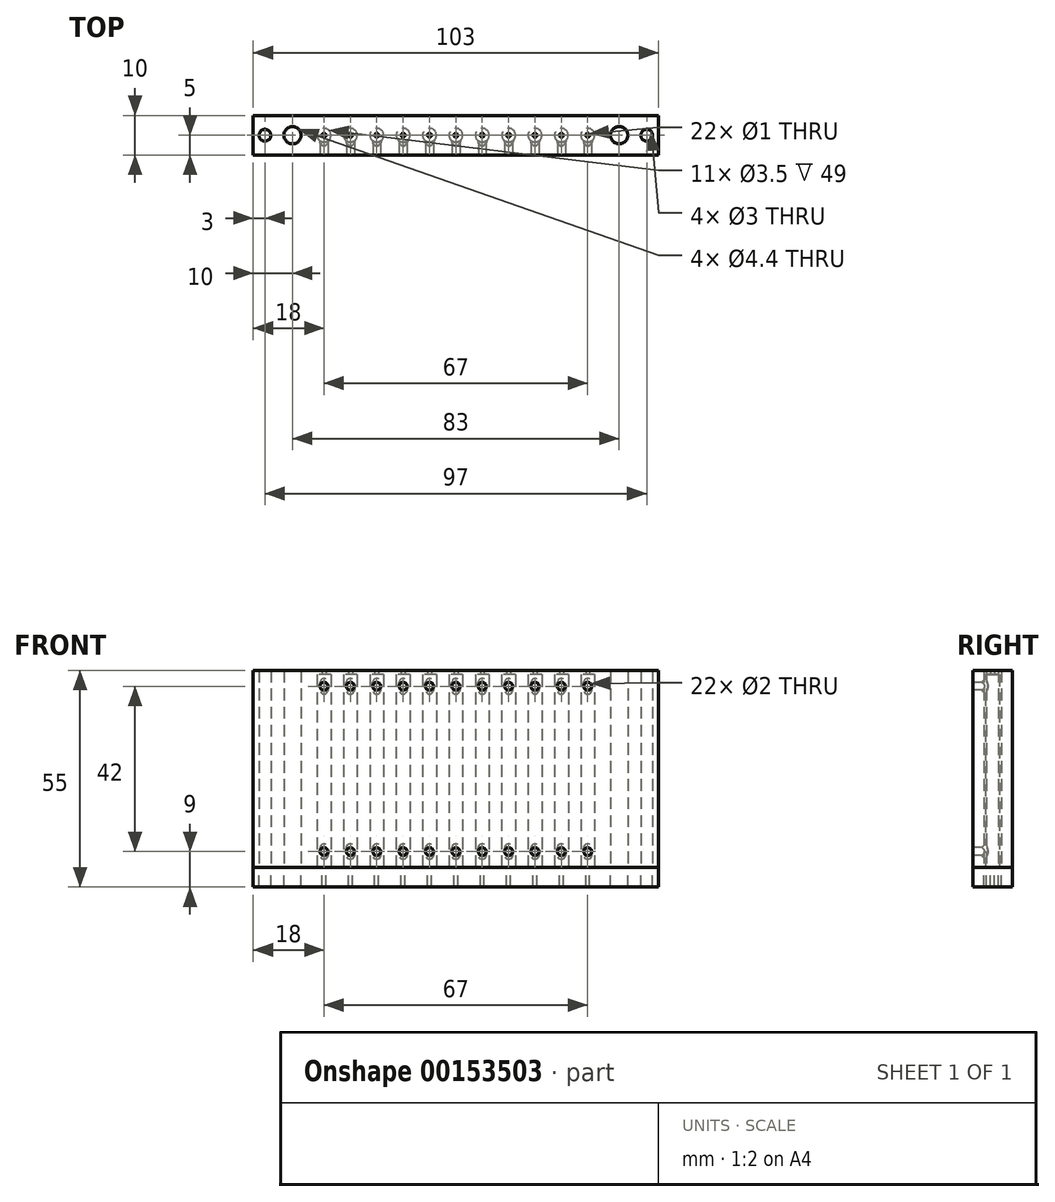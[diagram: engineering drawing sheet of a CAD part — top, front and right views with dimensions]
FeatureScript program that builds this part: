
annotation { "Feature Type Name" : "Feature", "Feature Type Description" : "" }
export const myFeature = defineFeature(function(context is Context, id is Id, definition is map)
    precondition{}
    {
        {
            var Q0;
            Q0=qCreatedBy(makeId("Top.planeOp"),FACE);
            var sketch = newSketch(context, id + "F0", { "sketchPlane" : qUnion([Q0])});
            skLineSegment(sketch, "E0.bottom", {"start": v(0, 0) * mm, "end": v(103, 0) * mm});
            skLineSegment(sketch, "E0.top", {"start": v(0, 10) * mm, "end": v(103, 10) * mm});
            skLineSegment(sketch, "E0.left", {"start": v(0, 0) * mm, "end": v(0, 10) * mm});
            skLineSegment(sketch, "E0.right", {"start": v(103, 0) * mm, "end": v(103, 10) * mm});
            skLineSegment(sketch, "E1", {"start": v(0, 5) * mm, "end": v(103, 5) * mm, "construction": true});
            skCircle(sketch, "E2", {"center": v(3, 5) * mm, "radius": 1.5 * mm});
            skCircle(sketch, "E3", {"center": v(10, 5) * mm, "radius": 2.2 * mm});
            skCircle(sketch, "E4", {"center": v(18, 5) * mm, "radius": 0.5 * mm});
            skLineSegment(sketch, "E5", {"start": v(51.5, 10) * mm, "end": v(51.5, 0) * mm, "construction": true});
            skCircle(sketch, "E6.MirrorC", {"center": v(93, 5) * mm, "radius": 2.2 * mm});
            skCircle(sketch, "E7.MirrorC", {"center": v(100, 5) * mm, "radius": 1.5 * mm});
            skCircle(sketch, "E8.1.0.0", {"center": v(24.7, 5) * mm, "radius": 0.5 * mm});
            skCircle(sketch, "E8.2.0.0", {"center": v(31.4, 5) * mm, "radius": 0.5 * mm});
            skCircle(sketch, "E8.3.0.0", {"center": v(38.1, 5) * mm, "radius": 0.5 * mm});
            skCircle(sketch, "E8.4.0.0", {"center": v(44.8, 5) * mm, "radius": 0.5 * mm});
            skCircle(sketch, "E8.5.0.0", {"center": v(51.5, 5) * mm, "radius": 0.5 * mm});
            skCircle(sketch, "E8.6.0.0", {"center": v(58.2, 5) * mm, "radius": 0.5 * mm});
            skCircle(sketch, "E8.7.0.0", {"center": v(64.9, 5) * mm, "radius": 0.5 * mm});
            skCircle(sketch, "E8.8.0.0", {"center": v(71.6, 5) * mm, "radius": 0.5 * mm});
            skCircle(sketch, "E8.9.0.0", {"center": v(78.3, 5) * mm, "radius": 0.5 * mm});
            skCircle(sketch, "E8.10.0.0", {"center": v(85, 5) * mm, "radius": 0.5 * mm});
            skLineSegment(sketch, "E8.direction1", {"start": v(17, 5) * mm, "end": v(24, 5) * mm, "construction": true});
            skCircle(sketch, "E9", {"center": v(10, 5) * mm, "radius": 5 * mm, "construction": true});
            skCircle(sketch, "E10", {"center": v(93, 5) * mm, "radius": 5 * mm, "construction": true});
            skSolve(sketch);
        }
        {
            var Q0;
            Q0=makeQuery(id+"F0.imprint","IMPRINT",FACE,{"disambiguationData":[TD([[makeQuery(id+"F0.imprint","IMPRINT",EDGE,{"derivedFrom":sQuery(id+"F0.wireOp",EDGE,"E0.bottom")}),1.0]])]});
            extrude(context, id + "F1", {"entities" : qUnion([Q0]), "depth" : 50 * mm});
        }
        {
            var Q0;
            Q0=makeQuery(id+"F0.imprint","IMPRINT",FACE,{"disambiguationData":[TD([[makeQuery(id+"F0.imprint","IMPRINT",EDGE,{"derivedFrom":sQuery(id+"F0.wireOp",EDGE,"E0.bottom")}),1.0]])]});
            var sketch = newSketch(context, id + "F2", { "sketchPlane" : qUnion([Q0])});
            skPoint(sketch, "E11.0", {"position": v(18, 5) * mm});
            skCircle(sketch, "E12", {"center": v(18, 5) * mm, "radius": 1.75 * mm});
            skCircle(sketch, "E13.1.0.0", {"center": v(24.7, 5) * mm, "radius": 1.75 * mm});
            skCircle(sketch, "E13.2.0.0", {"center": v(31.4, 5) * mm, "radius": 1.75 * mm});
            skCircle(sketch, "E13.3.0.0", {"center": v(38.1, 5) * mm, "radius": 1.75 * mm});
            skCircle(sketch, "E13.4.0.0", {"center": v(44.8, 5) * mm, "radius": 1.75 * mm});
            skCircle(sketch, "E13.5.0.0", {"center": v(51.5, 5) * mm, "radius": 1.75 * mm});
            skCircle(sketch, "E13.6.0.0", {"center": v(58.2, 5) * mm, "radius": 1.75 * mm});
            skCircle(sketch, "E13.7.0.0", {"center": v(64.9, 5) * mm, "radius": 1.75 * mm});
            skCircle(sketch, "E13.8.0.0", {"center": v(71.6, 5) * mm, "radius": 1.75 * mm});
            skCircle(sketch, "E13.9.0.0", {"center": v(78.3, 5) * mm, "radius": 1.75 * mm});
            skCircle(sketch, "E13.10.0.0", {"center": v(85, 5) * mm, "radius": 1.75 * mm});
            skLineSegment(sketch, "E13.direction1", {"start": v(18, 5) * mm, "end": v(24.7, 5) * mm, "construction": true});
            skSolve(sketch);
        }
        {
            var Q0;
            Q0 = qSketchRegion(id + "F2", true);
            extrude(context, id + "F3", {"entities" : qUnion([Q0]), "operationType" : NewBodyOperationType.REMOVE, "depth" : 49 * mm});
        }
        {
            var Q0;
            Q0=makeQuery(id+"F0.imprint","IMPRINT",FACE,{"disambiguationData":[TD([[makeQuery(id+"F0.imprint","IMPRINT",EDGE,{"derivedFrom":sQuery(id+"F0.wireOp",EDGE,"E0.bottom")}),1.0]])]});
            extrude(context, id + "F4", {"entities" : qUnion([Q0]), "oppositeDirection" : true, "depth" : 5 * mm});
        }
        {
            var Q0;
            Q0=makeQuery(id+"F1.opExtrude","SWEPT_FACE",FACE,{"disambiguationData":[OSD([sQuery(id+"F0.wireOp",EDGE,"E0.bottom")])]});
            var sketch = newSketch(context, id + "F5", { "sketchPlane" : qUnion([Q0])});
            skLineSegment(sketch, "E14.bottom", {"start": v(103, 50) * mm, "end": v(85, 50) * mm, "construction": true});
            skLineSegment(sketch, "E14.top", {"start": v(103, 46) * mm, "end": v(85, 46) * mm, "construction": true});
            skLineSegment(sketch, "E14.left", {"start": v(103, 50) * mm, "end": v(103, 46) * mm, "construction": true});
            skLineSegment(sketch, "E14.right", {"start": v(85, 50) * mm, "end": v(85, 46) * mm, "construction": true});
            skLineSegment(sketch, "E15", {"start": v(103, 25) * mm, "end": v(0, 25) * mm, "construction": true});
            skCircle(sketch, "E16", {"center": v(85, 46) * mm, "radius": 1 * mm});
            skCircle(sketch, "E17.0.1.0", {"center": v(85, 4) * mm, "radius": 1 * mm});
            skCircle(sketch, "E17.1.0.0", {"center": v(78.3, 46) * mm, "radius": 1 * mm});
            skCircle(sketch, "E17.1.1.0", {"center": v(78.3, 4) * mm, "radius": 1 * mm});
            skCircle(sketch, "E17.2.0.0", {"center": v(71.6, 46) * mm, "radius": 1 * mm});
            skCircle(sketch, "E17.2.1.0", {"center": v(71.6, 4) * mm, "radius": 1 * mm});
            skCircle(sketch, "E17.3.0.0", {"center": v(64.9, 46) * mm, "radius": 1 * mm});
            skCircle(sketch, "E17.3.1.0", {"center": v(64.9, 4) * mm, "radius": 1 * mm});
            skCircle(sketch, "E17.4.0.0", {"center": v(58.2, 46) * mm, "radius": 1 * mm});
            skCircle(sketch, "E17.4.1.0", {"center": v(58.2, 4) * mm, "radius": 1 * mm});
            skCircle(sketch, "E17.5.0.0", {"center": v(51.5, 46) * mm, "radius": 1 * mm});
            skCircle(sketch, "E17.5.1.0", {"center": v(51.5, 4) * mm, "radius": 1 * mm});
            skCircle(sketch, "E17.6.0.0", {"center": v(44.8, 46) * mm, "radius": 1 * mm});
            skCircle(sketch, "E17.6.1.0", {"center": v(44.8, 4) * mm, "radius": 1 * mm});
            skCircle(sketch, "E17.7.0.0", {"center": v(38.1, 46) * mm, "radius": 1 * mm});
            skCircle(sketch, "E17.7.1.0", {"center": v(38.1, 4) * mm, "radius": 1 * mm});
            skCircle(sketch, "E17.8.0.0", {"center": v(31.4, 46) * mm, "radius": 1 * mm});
            skCircle(sketch, "E17.8.1.0", {"center": v(31.4, 4) * mm, "radius": 1 * mm});
            skCircle(sketch, "E17.9.0.0", {"center": v(24.7, 46) * mm, "radius": 1 * mm});
            skCircle(sketch, "E17.9.1.0", {"center": v(24.7, 4) * mm, "radius": 1 * mm});
            skCircle(sketch, "E17.10.0.0", {"center": v(18, 46) * mm, "radius": 1 * mm});
            skCircle(sketch, "E17.10.1.0", {"center": v(18, 4) * mm, "radius": 1 * mm});
            skLineSegment(sketch, "E17.direction1", {"start": v(85, 46) * mm, "end": v(78.3, 46) * mm, "construction": true});
            skLineSegment(sketch, "E17.direction2", {"start": v(85, 46) * mm, "end": v(85, 4) * mm, "construction": true});
            skSolve(sketch);
        }
        {
            var Q0;
            Q0 = qSketchRegion(id + "F5", true);
            extrude(context, id + "F6", {"entities" : qUnion([Q0]), "operationType" : NewBodyOperationType.REMOVE, "oppositeDirection" : true, "depth" : 5 * mm});
        }
        {
            var Q0;
            Q0=makeQuery(id+"F6.boolean.opBoolean","COPY",EDGE,{"derivedFrom":makeQuery(id+"F6.opExtrude","CAP_EDGE",EDGE,{"disambiguationData":[OSD([sQuery(id+"F5.wireOp",EDGE,"E17.0.1.0")])],"isStart":true})});
            var Q1;
            Q1=makeQuery(id+"F6.boolean.opBoolean","COPY",EDGE,{"derivedFrom":makeQuery(id+"F6.opExtrude","CAP_EDGE",EDGE,{"disambiguationData":[OSD([sQuery(id+"F5.wireOp",EDGE,"E17.1.1.0")])],"isStart":true})});
            var Q2;
            Q2=makeQuery(id+"F6.boolean.opBoolean","COPY",EDGE,{"derivedFrom":makeQuery(id+"F6.opExtrude","CAP_EDGE",EDGE,{"disambiguationData":[OSD([sQuery(id+"F5.wireOp",EDGE,"E17.2.1.0")])],"isStart":true})});
            var Q3;
            Q3=makeQuery(id+"F6.boolean.opBoolean","INTERSECT",EDGE,{"derivedFrom":[makeQuery(id+"F3.boolean.opBoolean","COPY",FACE,{"derivedFrom":makeQuery(id+"F3.opExtrude","SWEPT_FACE",FACE,{"disambiguationData":[OSD([sQuery(id+"F2.wireOp",EDGE,"E13.10.0.0")])]})}),makeQuery(id+"F6.opExtrude","SWEPT_FACE",FACE,{"disambiguationData":[OSD([sQuery(id+"F5.wireOp",EDGE,"E17.0.1.0")])]})]});
            var Q4;
            Q4=makeQuery(id+"F6.boolean.opBoolean","INTERSECT",EDGE,{"derivedFrom":[makeQuery(id+"F3.boolean.opBoolean","COPY",FACE,{"derivedFrom":makeQuery(id+"F3.opExtrude","SWEPT_FACE",FACE,{"disambiguationData":[OSD([sQuery(id+"F2.wireOp",EDGE,"E13.9.0.0")])]})}),makeQuery(id+"F6.opExtrude","SWEPT_FACE",FACE,{"disambiguationData":[OSD([sQuery(id+"F5.wireOp",EDGE,"E17.1.1.0")])]})]});
            var Q5;
            Q5=makeQuery(id+"F6.boolean.opBoolean","INTERSECT",EDGE,{"derivedFrom":[makeQuery(id+"F3.boolean.opBoolean","COPY",FACE,{"derivedFrom":makeQuery(id+"F3.opExtrude","SWEPT_FACE",FACE,{"disambiguationData":[OSD([sQuery(id+"F2.wireOp",EDGE,"E13.8.0.0")])]})}),makeQuery(id+"F6.opExtrude","SWEPT_FACE",FACE,{"disambiguationData":[OSD([sQuery(id+"F5.wireOp",EDGE,"E17.2.1.0")])]})]});
            var Q6;
            Q6=makeQuery(id+"F6.boolean.opBoolean","COPY",EDGE,{"derivedFrom":makeQuery(id+"F6.opExtrude","CAP_EDGE",EDGE,{"disambiguationData":[OSD([sQuery(id+"F5.wireOp",EDGE,"E17.3.1.0")])],"isStart":true})});
            var Q7;
            Q7=makeQuery(id+"F6.boolean.opBoolean","COPY",EDGE,{"derivedFrom":makeQuery(id+"F6.opExtrude","CAP_EDGE",EDGE,{"disambiguationData":[OSD([sQuery(id+"F5.wireOp",EDGE,"E17.4.1.0")])],"isStart":true})});
            var Q8;
            Q8=makeQuery(id+"F6.boolean.opBoolean","INTERSECT",EDGE,{"derivedFrom":[makeQuery(id+"F3.boolean.opBoolean","COPY",FACE,{"derivedFrom":makeQuery(id+"F3.opExtrude","SWEPT_FACE",FACE,{"disambiguationData":[OSD([sQuery(id+"F2.wireOp",EDGE,"E13.7.0.0")])]})}),makeQuery(id+"F6.opExtrude","SWEPT_FACE",FACE,{"disambiguationData":[OSD([sQuery(id+"F5.wireOp",EDGE,"E17.3.1.0")])]})]});
            var Q9;
            Q9=makeQuery(id+"F6.boolean.opBoolean","INTERSECT",EDGE,{"derivedFrom":[makeQuery(id+"F3.boolean.opBoolean","COPY",FACE,{"derivedFrom":makeQuery(id+"F3.opExtrude","SWEPT_FACE",FACE,{"disambiguationData":[OSD([sQuery(id+"F2.wireOp",EDGE,"E13.6.0.0")])]})}),makeQuery(id+"F6.opExtrude","SWEPT_FACE",FACE,{"disambiguationData":[OSD([sQuery(id+"F5.wireOp",EDGE,"E17.4.1.0")])]})]});
            var Q10;
            Q10=makeQuery(id+"F6.boolean.opBoolean","COPY",EDGE,{"derivedFrom":makeQuery(id+"F6.opExtrude","CAP_EDGE",EDGE,{"disambiguationData":[OSD([sQuery(id+"F5.wireOp",EDGE,"E17.1.0.0")])],"isStart":true})});
            var Q11;
            Q11=makeQuery(id+"F6.boolean.opBoolean","COPY",EDGE,{"derivedFrom":makeQuery(id+"F6.opExtrude","CAP_EDGE",EDGE,{"disambiguationData":[OSD([sQuery(id+"F5.wireOp",EDGE,"E17.7.0.0")])],"isStart":true})});
            var Q12;
            Q12=makeQuery(id+"F6.boolean.opBoolean","COPY",EDGE,{"derivedFrom":makeQuery(id+"F6.opExtrude","CAP_EDGE",EDGE,{"disambiguationData":[OSD([sQuery(id+"F5.wireOp",EDGE,"E16")])],"isStart":true})});
            var Q13;
            Q13=makeQuery(id+"F6.boolean.opBoolean","COPY",EDGE,{"derivedFrom":makeQuery(id+"F6.opExtrude","CAP_EDGE",EDGE,{"disambiguationData":[OSD([sQuery(id+"F5.wireOp",EDGE,"E17.2.0.0")])],"isStart":true})});
            var Q14;
            Q14=makeQuery(id+"F6.boolean.opBoolean","COPY",EDGE,{"derivedFrom":makeQuery(id+"F6.opExtrude","CAP_EDGE",EDGE,{"disambiguationData":[OSD([sQuery(id+"F5.wireOp",EDGE,"E17.3.0.0")])],"isStart":true})});
            var Q15;
            Q15=makeQuery(id+"F6.boolean.opBoolean","COPY",EDGE,{"derivedFrom":makeQuery(id+"F6.opExtrude","CAP_EDGE",EDGE,{"disambiguationData":[OSD([sQuery(id+"F5.wireOp",EDGE,"E17.4.0.0")])],"isStart":true})});
            var Q16;
            Q16=makeQuery(id+"F6.boolean.opBoolean","COPY",EDGE,{"derivedFrom":makeQuery(id+"F6.opExtrude","CAP_EDGE",EDGE,{"disambiguationData":[OSD([sQuery(id+"F5.wireOp",EDGE,"E17.5.0.0")])],"isStart":true})});
            var Q17;
            Q17=makeQuery(id+"F6.boolean.opBoolean","COPY",EDGE,{"derivedFrom":makeQuery(id+"F6.opExtrude","CAP_EDGE",EDGE,{"disambiguationData":[OSD([sQuery(id+"F5.wireOp",EDGE,"E17.6.0.0")])],"isStart":true})});
            var Q18;
            Q18=makeQuery(id+"F6.boolean.opBoolean","COPY",EDGE,{"derivedFrom":makeQuery(id+"F6.opExtrude","CAP_EDGE",EDGE,{"disambiguationData":[OSD([sQuery(id+"F5.wireOp",EDGE,"E17.8.0.0")])],"isStart":true})});
            var Q19;
            Q19=makeQuery(id+"F6.boolean.opBoolean","COPY",EDGE,{"derivedFrom":makeQuery(id+"F6.opExtrude","CAP_EDGE",EDGE,{"disambiguationData":[OSD([sQuery(id+"F5.wireOp",EDGE,"E17.9.0.0")])],"isStart":true})});
            var Q20;
            Q20=makeQuery(id+"F6.boolean.opBoolean","COPY",EDGE,{"derivedFrom":makeQuery(id+"F6.opExtrude","CAP_EDGE",EDGE,{"disambiguationData":[OSD([sQuery(id+"F5.wireOp",EDGE,"E17.10.0.0")])],"isStart":true})});
            var Q21;
            Q21=makeQuery(id+"F6.boolean.opBoolean","INTERSECT",EDGE,{"derivedFrom":[makeQuery(id+"F3.boolean.opBoolean","COPY",FACE,{"derivedFrom":makeQuery(id+"F3.opExtrude","SWEPT_FACE",FACE,{"disambiguationData":[OSD([sQuery(id+"F2.wireOp",EDGE,"E13.1.0.0")])]})}),makeQuery(id+"F6.opExtrude","SWEPT_FACE",FACE,{"disambiguationData":[OSD([sQuery(id+"F5.wireOp",EDGE,"E17.9.0.0")])]})]});
            var Q22;
            Q22=makeQuery(id+"F6.boolean.opBoolean","INTERSECT",EDGE,{"derivedFrom":[makeQuery(id+"F3.boolean.opBoolean","COPY",FACE,{"derivedFrom":makeQuery(id+"F3.opExtrude","SWEPT_FACE",FACE,{"disambiguationData":[OSD([sQuery(id+"F2.wireOp",EDGE,"E13.6.0.0")])]})}),makeQuery(id+"F6.opExtrude","SWEPT_FACE",FACE,{"disambiguationData":[OSD([sQuery(id+"F5.wireOp",EDGE,"E17.4.0.0")])]})]});
            var Q23;
            Q23=makeQuery(id+"F6.boolean.opBoolean","INTERSECT",EDGE,{"derivedFrom":[makeQuery(id+"F3.boolean.opBoolean","COPY",FACE,{"derivedFrom":makeQuery(id+"F3.opExtrude","SWEPT_FACE",FACE,{"disambiguationData":[OSD([sQuery(id+"F2.wireOp",EDGE,"E13.5.0.0")])]})}),makeQuery(id+"F6.opExtrude","SWEPT_FACE",FACE,{"disambiguationData":[OSD([sQuery(id+"F5.wireOp",EDGE,"E17.5.0.0")])]})]});
            var Q24;
            Q24=makeQuery(id+"F6.boolean.opBoolean","INTERSECT",EDGE,{"derivedFrom":[makeQuery(id+"F3.boolean.opBoolean","COPY",FACE,{"derivedFrom":makeQuery(id+"F3.opExtrude","SWEPT_FACE",FACE,{"disambiguationData":[OSD([sQuery(id+"F2.wireOp",EDGE,"E13.4.0.0")])]})}),makeQuery(id+"F6.opExtrude","SWEPT_FACE",FACE,{"disambiguationData":[OSD([sQuery(id+"F5.wireOp",EDGE,"E17.6.0.0")])]})]});
            var Q25;
            Q25=makeQuery(id+"F6.boolean.opBoolean","INTERSECT",EDGE,{"derivedFrom":[makeQuery(id+"F3.boolean.opBoolean","COPY",FACE,{"derivedFrom":makeQuery(id+"F3.opExtrude","SWEPT_FACE",FACE,{"disambiguationData":[OSD([sQuery(id+"F2.wireOp",EDGE,"E13.3.0.0")])]})}),makeQuery(id+"F6.opExtrude","SWEPT_FACE",FACE,{"disambiguationData":[OSD([sQuery(id+"F5.wireOp",EDGE,"E17.7.0.0")])]})]});
            var Q26;
            Q26=makeQuery(id+"F6.boolean.opBoolean","INTERSECT",EDGE,{"derivedFrom":[makeQuery(id+"F3.boolean.opBoolean","COPY",FACE,{"derivedFrom":makeQuery(id+"F3.opExtrude","SWEPT_FACE",FACE,{"disambiguationData":[OSD([sQuery(id+"F2.wireOp",EDGE,"E13.10.0.0")])]})}),makeQuery(id+"F6.opExtrude","SWEPT_FACE",FACE,{"disambiguationData":[OSD([sQuery(id+"F5.wireOp",EDGE,"E16")])]})]});
            var Q27;
            Q27=makeQuery(id+"F6.boolean.opBoolean","INTERSECT",EDGE,{"derivedFrom":[makeQuery(id+"F3.boolean.opBoolean","COPY",FACE,{"derivedFrom":makeQuery(id+"F3.opExtrude","SWEPT_FACE",FACE,{"disambiguationData":[OSD([sQuery(id+"F2.wireOp",EDGE,"E13.2.0.0")])]})}),makeQuery(id+"F6.opExtrude","SWEPT_FACE",FACE,{"disambiguationData":[OSD([sQuery(id+"F5.wireOp",EDGE,"E17.8.0.0")])]})]});
            var Q28;
            Q28=makeQuery(id+"F6.boolean.opBoolean","INTERSECT",EDGE,{"derivedFrom":[makeQuery(id+"F3.boolean.opBoolean","COPY",FACE,{"derivedFrom":makeQuery(id+"F3.opExtrude","SWEPT_FACE",FACE,{"disambiguationData":[OSD([sQuery(id+"F2.wireOp",EDGE,"E13.9.0.0")])]})}),makeQuery(id+"F6.opExtrude","SWEPT_FACE",FACE,{"disambiguationData":[OSD([sQuery(id+"F5.wireOp",EDGE,"E17.1.0.0")])]})]});
            var Q29;
            Q29=makeQuery(id+"F6.boolean.opBoolean","INTERSECT",EDGE,{"derivedFrom":[makeQuery(id+"F3.boolean.opBoolean","COPY",FACE,{"derivedFrom":makeQuery(id+"F3.opExtrude","SWEPT_FACE",FACE,{"disambiguationData":[OSD([sQuery(id+"F2.wireOp",EDGE,"E13.8.0.0")])]})}),makeQuery(id+"F6.opExtrude","SWEPT_FACE",FACE,{"disambiguationData":[OSD([sQuery(id+"F5.wireOp",EDGE,"E17.2.0.0")])]})]});
            var Q30;
            Q30=makeQuery(id+"F6.boolean.opBoolean","INTERSECT",EDGE,{"derivedFrom":[makeQuery(id+"F3.boolean.opBoolean","COPY",FACE,{"derivedFrom":makeQuery(id+"F3.opExtrude","SWEPT_FACE",FACE,{"disambiguationData":[OSD([sQuery(id+"F2.wireOp",EDGE,"E12")])]})}),makeQuery(id+"F6.opExtrude","SWEPT_FACE",FACE,{"disambiguationData":[OSD([sQuery(id+"F5.wireOp",EDGE,"E17.10.0.0")])]})]});
            var Q31;
            Q31=makeQuery(id+"F6.boolean.opBoolean","INTERSECT",EDGE,{"derivedFrom":[makeQuery(id+"F3.boolean.opBoolean","COPY",FACE,{"derivedFrom":makeQuery(id+"F3.opExtrude","SWEPT_FACE",FACE,{"disambiguationData":[OSD([sQuery(id+"F2.wireOp",EDGE,"E13.7.0.0")])]})}),makeQuery(id+"F6.opExtrude","SWEPT_FACE",FACE,{"disambiguationData":[OSD([sQuery(id+"F5.wireOp",EDGE,"E17.3.0.0")])]})]});
            var Q32;
            Q32=makeQuery(id+"F6.boolean.opBoolean","COPY",EDGE,{"derivedFrom":makeQuery(id+"F6.opExtrude","CAP_EDGE",EDGE,{"disambiguationData":[OSD([sQuery(id+"F5.wireOp",EDGE,"E17.6.1.0")])],"isStart":true})});
            var Q33;
            Q33=makeQuery(id+"F6.boolean.opBoolean","COPY",EDGE,{"derivedFrom":makeQuery(id+"F6.opExtrude","CAP_EDGE",EDGE,{"disambiguationData":[OSD([sQuery(id+"F5.wireOp",EDGE,"E17.7.1.0")])],"isStart":true})});
            var Q34;
            Q34=makeQuery(id+"F6.boolean.opBoolean","COPY",EDGE,{"derivedFrom":makeQuery(id+"F6.opExtrude","CAP_EDGE",EDGE,{"disambiguationData":[OSD([sQuery(id+"F5.wireOp",EDGE,"E17.5.1.0")])],"isStart":true})});
            var Q35;
            Q35=makeQuery(id+"F6.boolean.opBoolean","COPY",EDGE,{"derivedFrom":makeQuery(id+"F6.opExtrude","CAP_EDGE",EDGE,{"disambiguationData":[OSD([sQuery(id+"F5.wireOp",EDGE,"E17.8.1.0")])],"isStart":true})});
            var Q36;
            Q36=makeQuery(id+"F6.boolean.opBoolean","COPY",EDGE,{"derivedFrom":makeQuery(id+"F6.opExtrude","CAP_EDGE",EDGE,{"disambiguationData":[OSD([sQuery(id+"F5.wireOp",EDGE,"E17.9.1.0")])],"isStart":true})});
            var Q37;
            Q37=makeQuery(id+"F6.boolean.opBoolean","COPY",EDGE,{"derivedFrom":makeQuery(id+"F6.opExtrude","CAP_EDGE",EDGE,{"disambiguationData":[OSD([sQuery(id+"F5.wireOp",EDGE,"E17.10.1.0")])],"isStart":true})});
            var Q38;
            Q38=makeQuery(id+"F6.boolean.opBoolean","INTERSECT",EDGE,{"derivedFrom":[makeQuery(id+"F3.boolean.opBoolean","COPY",FACE,{"derivedFrom":makeQuery(id+"F3.opExtrude","SWEPT_FACE",FACE,{"disambiguationData":[OSD([sQuery(id+"F2.wireOp",EDGE,"E13.5.0.0")])]})}),makeQuery(id+"F6.opExtrude","SWEPT_FACE",FACE,{"disambiguationData":[OSD([sQuery(id+"F5.wireOp",EDGE,"E17.5.1.0")])]})]});
            var Q39;
            Q39=makeQuery(id+"F6.boolean.opBoolean","INTERSECT",EDGE,{"derivedFrom":[makeQuery(id+"F3.boolean.opBoolean","COPY",FACE,{"derivedFrom":makeQuery(id+"F3.opExtrude","SWEPT_FACE",FACE,{"disambiguationData":[OSD([sQuery(id+"F2.wireOp",EDGE,"E13.4.0.0")])]})}),makeQuery(id+"F6.opExtrude","SWEPT_FACE",FACE,{"disambiguationData":[OSD([sQuery(id+"F5.wireOp",EDGE,"E17.6.1.0")])]})]});
            var Q40;
            Q40=makeQuery(id+"F6.boolean.opBoolean","INTERSECT",EDGE,{"derivedFrom":[makeQuery(id+"F3.boolean.opBoolean","COPY",FACE,{"derivedFrom":makeQuery(id+"F3.opExtrude","SWEPT_FACE",FACE,{"disambiguationData":[OSD([sQuery(id+"F2.wireOp",EDGE,"E13.3.0.0")])]})}),makeQuery(id+"F6.opExtrude","SWEPT_FACE",FACE,{"disambiguationData":[OSD([sQuery(id+"F5.wireOp",EDGE,"E17.7.1.0")])]})]});
            var Q41;
            Q41=makeQuery(id+"F6.boolean.opBoolean","INTERSECT",EDGE,{"derivedFrom":[makeQuery(id+"F3.boolean.opBoolean","COPY",FACE,{"derivedFrom":makeQuery(id+"F3.opExtrude","SWEPT_FACE",FACE,{"disambiguationData":[OSD([sQuery(id+"F2.wireOp",EDGE,"E13.2.0.0")])]})}),makeQuery(id+"F6.opExtrude","SWEPT_FACE",FACE,{"disambiguationData":[OSD([sQuery(id+"F5.wireOp",EDGE,"E17.8.1.0")])]})]});
            var Q42;
            Q42=makeQuery(id+"F6.boolean.opBoolean","INTERSECT",EDGE,{"derivedFrom":[makeQuery(id+"F3.boolean.opBoolean","COPY",FACE,{"derivedFrom":makeQuery(id+"F3.opExtrude","SWEPT_FACE",FACE,{"disambiguationData":[OSD([sQuery(id+"F2.wireOp",EDGE,"E13.1.0.0")])]})}),makeQuery(id+"F6.opExtrude","SWEPT_FACE",FACE,{"disambiguationData":[OSD([sQuery(id+"F5.wireOp",EDGE,"E17.9.1.0")])]})]});
            var Q43;
            Q43=makeQuery(id+"F6.boolean.opBoolean","INTERSECT",EDGE,{"derivedFrom":[makeQuery(id+"F3.boolean.opBoolean","COPY",FACE,{"derivedFrom":makeQuery(id+"F3.opExtrude","SWEPT_FACE",FACE,{"disambiguationData":[OSD([sQuery(id+"F2.wireOp",EDGE,"E12")])]})}),makeQuery(id+"F6.opExtrude","SWEPT_FACE",FACE,{"disambiguationData":[OSD([sQuery(id+"F5.wireOp",EDGE,"E17.10.1.0")])]})]});
            chamfer(context, id + "F7", {"entities" : qUnion([Q0, Q1, Q2, Q3, Q4, Q5, Q6, Q7, Q8, Q9, Q10, Q11, Q12, Q13, Q14, Q15, Q16, Q17, Q18, Q19, Q20, Q21, Q22, Q23, Q24, Q25, Q26, Q27, Q28, Q29, Q30, Q31, Q32, Q33, Q34, Q35, Q36, Q37, Q38, Q39, Q40, Q41, Q42, Q43]), "width" : 1 * mm, "tangentPropagation" : true});
        }
    });
